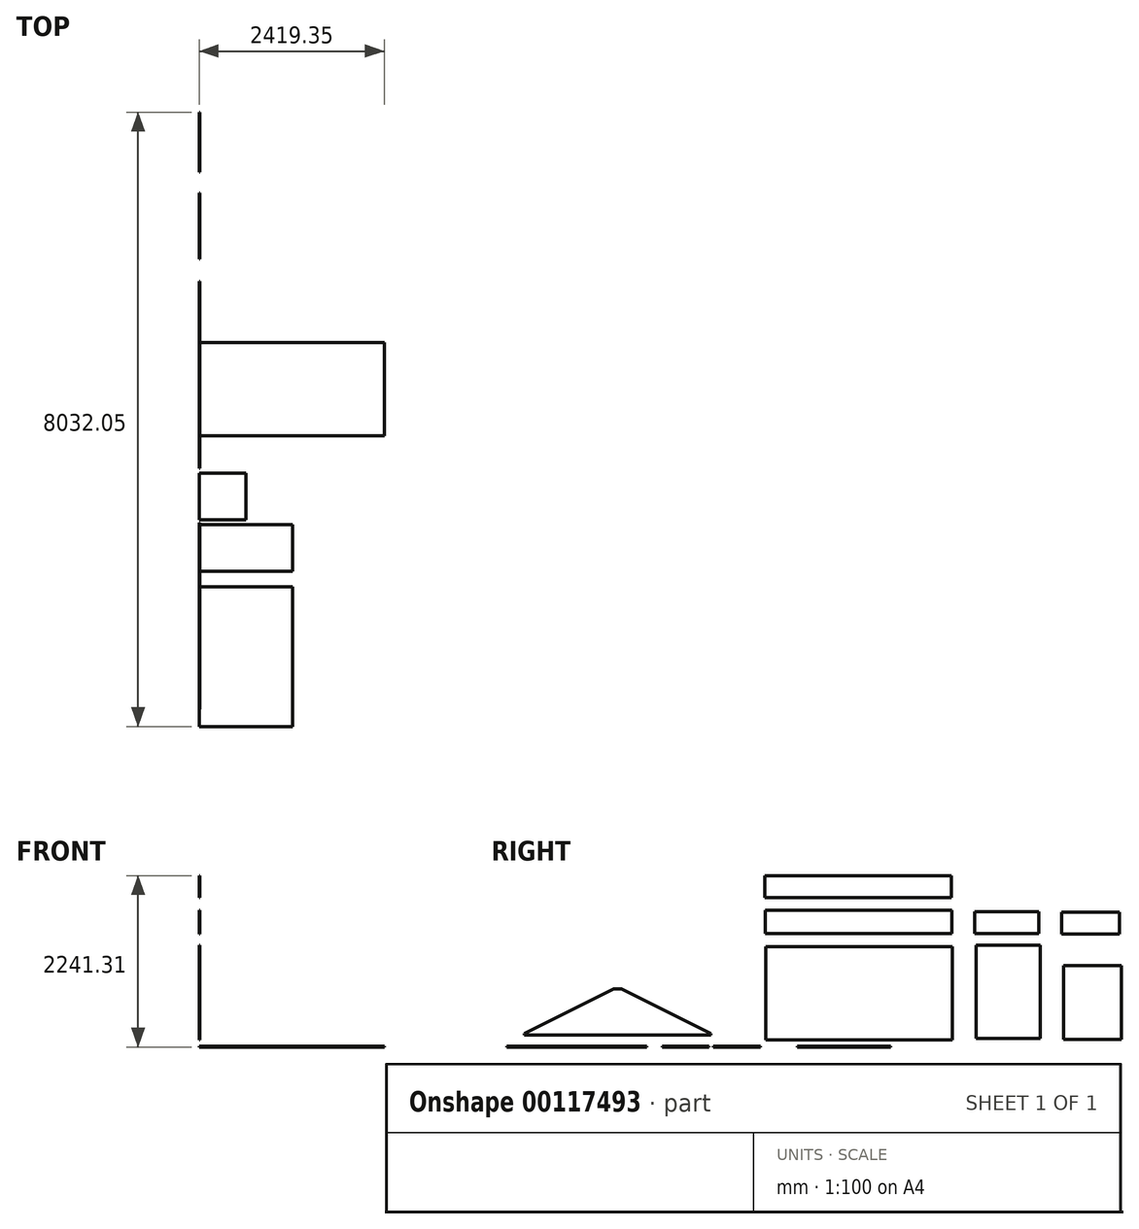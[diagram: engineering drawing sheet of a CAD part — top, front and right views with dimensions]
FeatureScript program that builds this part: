
annotation { "Feature Type Name" : "Feature", "Feature Type Description" : "" }
export const myFeature = defineFeature(function(context is Context, id is Id, definition is map)
    precondition{}
    {
        {
            var Q0;
            Q0=qCreatedBy(makeId("Top.planeOp"),FACE);
            var sketch = newSketch(context, id + "F0", { "sketchPlane" : qUnion([Q0])});
            skLineSegment(sketch, "E0.bottom", {"start": v(0, 0) * mm, "end": v(2419.35, 0) * mm});
            skLineSegment(sketch, "E0.top", {"start": v(0, -1219.2) * mm, "end": v(2419.35, -1219.2) * mm});
            skLineSegment(sketch, "E0.left", {"start": v(0, 0) * mm, "end": v(0, -1219.2) * mm});
            skLineSegment(sketch, "E0.right", {"start": v(2419.35, 0) * mm, "end": v(2419.35, -1219.2) * mm});
            skSolve(sketch);
        }
        {
            var Q0;
            Q0=makeQuery(id+"F0.imprint","IMPRINT",FACE,{"disambiguationData":[TD([[makeQuery(id+"F0.imprint","IMPRINT",EDGE,{"derivedFrom":sQuery(id+"F0.wireOp",EDGE,"E0.bottom")}),-1.0]])]});
            extrude(context, id + "F1", {"entities" : qUnion([Q0]), "depth" : 12.7 * mm});
        }
        {
            var Q0;
            Q0=qCreatedBy(makeId("Right.planeOp"),FACE);
            var sketch = newSketch(context, id + "F2", { "sketchPlane" : qUnion([Q0])});
            skLineSegment(sketch, "E1.bottom", {"start": v(-1635.37, 1309.76) * mm, "end": v(803.03, 1309.76) * mm});
            skLineSegment(sketch, "E1.top", {"start": v(-1635.37, 90.56) * mm, "end": v(803.03, 90.56) * mm});
            skLineSegment(sketch, "E1.left", {"start": v(-1635.37, 1309.76) * mm, "end": v(-1635.37, 90.56) * mm});
            skLineSegment(sketch, "E1.right", {"start": v(803.03, 1309.76) * mm, "end": v(803.03, 90.56) * mm});
            skSolve(sketch);
        }
        {
            var Q0;
            Q0=makeQuery(id+"F2.imprint","IMPRINT",FACE,{"disambiguationData":[TD([[makeQuery(id+"F2.imprint","IMPRINT",EDGE,{"derivedFrom":sQuery(id+"F2.wireOp",EDGE,"E1.bottom")}),-1.0]])]});
            extrude(context, id + "F3", {"entities" : qUnion([Q0]), "depth" : 9.52 * mm});
        }
        {
            var Q0;
            Q0=qCreatedBy(makeId("Right.planeOp"),FACE);
            var sketch = newSketch(context, id + "F4", { "sketchPlane" : qUnion([Q0])});
            skLineSegment(sketch, "E2.bottom", {"start": v(-1642.51, 1485.23) * mm, "end": v(795.89, 1485.23) * mm});
            skLineSegment(sketch, "E2.top", {"start": v(-1642.51, 1790.03) * mm, "end": v(795.89, 1790.03) * mm});
            skLineSegment(sketch, "E2.left", {"start": v(-1642.51, 1485.23) * mm, "end": v(-1642.51, 1790.03) * mm});
            skLineSegment(sketch, "E2.right", {"start": v(795.89, 1485.23) * mm, "end": v(795.89, 1790.03) * mm});
            skSolve(sketch);
        }
        {
            var Q0;
            Q0=makeQuery(id+"F4.imprint","IMPRINT",FACE,{"disambiguationData":[TD([[makeQuery(id+"F4.imprint","IMPRINT",EDGE,{"derivedFrom":sQuery(id+"F4.wireOp",EDGE,"E2.bottom")}),1.0]])]});
            extrude(context, id + "F5", {"entities" : qUnion([Q0]), "depth" : 9.52 * mm});
        }
        {
            var Q0;
            Q0=qCreatedBy(makeId("Right.planeOp"),FACE);
            var sketch = newSketch(context, id + "F6", { "sketchPlane" : qUnion([Q0])});
            skLineSegment(sketch, "E3.bottom", {"start": v(1117.42, 112.68) * mm, "end": v(1955.62, 112.68) * mm});
            skLineSegment(sketch, "E3.top", {"start": v(1117.42, 1331.88) * mm, "end": v(1955.62, 1331.88) * mm});
            skLineSegment(sketch, "E3.left", {"start": v(1117.42, 112.68) * mm, "end": v(1117.42, 1331.88) * mm});
            skLineSegment(sketch, "E3.right", {"start": v(1955.62, 112.68) * mm, "end": v(1955.62, 1331.88) * mm});
            skSolve(sketch);
        }
        {
            var Q0;
            Q0=makeQuery(id+"F6.imprint","IMPRINT",FACE,{"disambiguationData":[TD([[makeQuery(id+"F6.imprint","IMPRINT",EDGE,{"derivedFrom":sQuery(id+"F6.wireOp",EDGE,"E3.bottom")}),1.0]])]});
            extrude(context, id + "F7", {"entities" : qUnion([Q0]), "depth" : 9.52 * mm});
        }
        {
            var Q0;
            Q0=qCreatedBy(makeId("Right.planeOp"),FACE);
            var sketch = newSketch(context, id + "F8", { "sketchPlane" : qUnion([Q0])});
            skLineSegment(sketch, "E4.bottom", {"start": v(2256.7, 99.25) * mm, "end": v(3012.35, 99.25) * mm});
            skLineSegment(sketch, "E4.top", {"start": v(2256.7, 1064.45) * mm, "end": v(3012.35, 1064.45) * mm});
            skLineSegment(sketch, "E4.left", {"start": v(2256.7, 99.25) * mm, "end": v(2256.7, 1064.45) * mm});
            skLineSegment(sketch, "E4.right", {"start": v(3012.35, 99.25) * mm, "end": v(3012.35, 1064.45) * mm});
            skSolve(sketch);
        }
        {
            var Q0;
            Q0=makeQuery(id+"F8.imprint","IMPRINT",FACE,{"disambiguationData":[TD([[makeQuery(id+"F8.imprint","IMPRINT",EDGE,{"derivedFrom":sQuery(id+"F8.wireOp",EDGE,"E4.bottom")}),1.0]])]});
            extrude(context, id + "F9", {"entities" : qUnion([Q0]), "depth" : 9.52 * mm});
        }
        {
            var Q0;
            Q0=qCreatedBy(makeId("Right.planeOp"),FACE);
            var sketch = newSketch(context, id + "F10", { "sketchPlane" : qUnion([Q0])});
            skLineSegment(sketch, "E5.bottom", {"start": v(1095.24, 1484.8) * mm, "end": v(1933.44, 1484.8) * mm});
            skLineSegment(sketch, "E5.top", {"start": v(1095.24, 1770.56) * mm, "end": v(1933.44, 1770.56) * mm});
            skLineSegment(sketch, "E5.left", {"start": v(1095.24, 1484.8) * mm, "end": v(1095.24, 1770.56) * mm});
            skLineSegment(sketch, "E5.right", {"start": v(1933.44, 1484.8) * mm, "end": v(1933.44, 1770.56) * mm});
            skSolve(sketch);
        }
        {
            var Q0;
            Q0=makeQuery(id+"F10.imprint","IMPRINT",FACE,{"disambiguationData":[TD([[makeQuery(id+"F10.imprint","IMPRINT",EDGE,{"derivedFrom":sQuery(id+"F10.wireOp",EDGE,"E5.bottom")}),1.0]])]});
            extrude(context, id + "F11", {"entities" : qUnion([Q0]), "depth" : 9.52 * mm});
        }
        {
            var Q0;
            Q0=qCreatedBy(makeId("Right.planeOp"),FACE);
            var sketch = newSketch(context, id + "F12", { "sketchPlane" : qUnion([Q0])});
            skLineSegment(sketch, "E6.bottom", {"start": v(2231.6, 1474.91) * mm, "end": v(2987.25, 1474.91) * mm});
            skLineSegment(sketch, "E6.top", {"start": v(2231.6, 1760.66) * mm, "end": v(2987.25, 1760.66) * mm});
            skLineSegment(sketch, "E6.left", {"start": v(2231.6, 1474.91) * mm, "end": v(2231.6, 1760.66) * mm});
            skLineSegment(sketch, "E6.right", {"start": v(2987.25, 1474.91) * mm, "end": v(2987.25, 1760.66) * mm});
            skSolve(sketch);
        }
        {
            var Q0;
            Q0=makeQuery(id+"F12.imprint","IMPRINT",FACE,{"disambiguationData":[TD([[makeQuery(id+"F12.imprint","IMPRINT",EDGE,{"derivedFrom":sQuery(id+"F12.wireOp",EDGE,"E6.bottom")}),1.0]])]});
            extrude(context, id + "F13", {"entities" : qUnion([Q0]), "depth" : 9.52 * mm});
        }
        {
            var Q0;
            Q0=qCreatedBy(makeId("Top.planeOp"),FACE);
            var sketch = newSketch(context, id + "F14", { "sketchPlane" : qUnion([Q0])});
            skLineSegment(sketch, "E7.bottom", {"start": v(0, -2379.66) * mm, "end": v(1219.2, -2379.66) * mm});
            skLineSegment(sketch, "E7.top", {"start": v(0, -2989.26) * mm, "end": v(1219.2, -2989.26) * mm});
            skLineSegment(sketch, "E7.left", {"start": v(0, -2379.66) * mm, "end": v(0, -2989.26) * mm});
            skLineSegment(sketch, "E7.right", {"start": v(1219.2, -2379.66) * mm, "end": v(1219.2, -2989.26) * mm});
            skSolve(sketch);
        }
        {
            var Q0;
            Q0=qCreatedBy(makeId("Top.planeOp"),FACE);
            var sketch = newSketch(context, id + "F15", { "sketchPlane" : qUnion([Q0])});
            skLineSegment(sketch, "E8.bottom", {"start": v(0, -3190.9) * mm, "end": v(1219.2, -3190.9) * mm});
            skLineSegment(sketch, "E8.top", {"start": v(0, -5019.7) * mm, "end": v(1219.2, -5019.7) * mm});
            skLineSegment(sketch, "E8.left", {"start": v(0, -3190.9) * mm, "end": v(0, -5019.7) * mm});
            skLineSegment(sketch, "E8.right", {"start": v(1219.2, -3190.9) * mm, "end": v(1219.2, -5019.7) * mm});
            skSolve(sketch);
        }
        {
            var Q0;
            Q0=makeQuery(id+"F15.imprint","IMPRINT",FACE,{"disambiguationData":[TD([[makeQuery(id+"F15.imprint","IMPRINT",EDGE,{"derivedFrom":sQuery(id+"F15.wireOp",EDGE,"E8.bottom")}),-1.0]])]});
            extrude(context, id + "F16", {"entities" : qUnion([Q0]), "depth" : 9.52 * mm});
        }
        {
            var Q0;
            Q0=makeQuery(id+"F14.imprint","IMPRINT",FACE,{"disambiguationData":[TD([[makeQuery(id+"F14.imprint","IMPRINT",EDGE,{"derivedFrom":sQuery(id+"F14.wireOp",EDGE,"E7.bottom")}),-1.0]])]});
            extrude(context, id + "F17", {"entities" : qUnion([Q0]), "depth" : 9.52 * mm});
        }
        {
            var Q0;
            Q0=qCreatedBy(makeId("Top.planeOp"),FACE);
            var sketch = newSketch(context, id + "F18", { "sketchPlane" : qUnion([Q0])});
            skLineSegment(sketch, "E9.bottom", {"start": v(0, -2315.98) * mm, "end": v(609.6, -2315.98) * mm});
            skLineSegment(sketch, "E9.top", {"start": v(0, -1706.38) * mm, "end": v(609.6, -1706.38) * mm});
            skLineSegment(sketch, "E9.left", {"start": v(0, -2315.98) * mm, "end": v(0, -1706.38) * mm});
            skLineSegment(sketch, "E9.right", {"start": v(609.6, -2315.98) * mm, "end": v(609.6, -1706.38) * mm});
            skSolve(sketch);
        }
        {
            var Q0;
            Q0=makeQuery(id+"F18.imprint","IMPRINT",FACE,{"disambiguationData":[TD([[makeQuery(id+"F18.imprint","IMPRINT",EDGE,{"derivedFrom":sQuery(id+"F18.wireOp",EDGE,"E9.bottom")}),1.0]])]});
            extrude(context, id + "F19", {"entities" : qUnion([Q0]), "depth" : 9.52 * mm});
        }
        {
            var Q0;
            Q0=qCreatedBy(makeId("Right.planeOp"),FACE);
            var sketch = newSketch(context, id + "F20", { "sketchPlane" : qUnion([Q0])});
            skLineSegment(sketch, "E10", {"start": v(-4790.86, 176.8) * mm, "end": v(-3624.12, 758.52) * mm});
            skLineSegment(sketch, "E11", {"start": v(-3519.21, 758.52) * mm, "end": v(-2352.46, 176.8) * mm});
            skLineSegment(sketch, "E12", {"start": v(-4790.86, 176.8) * mm, "end": v(-4790.86, 157.75) * mm});
            skLineSegment(sketch, "E13", {"start": v(-4790.86, 157.75) * mm, "end": v(-2352.46, 157.75) * mm});
            skLineSegment(sketch, "E14", {"start": v(-2352.46, 157.75) * mm, "end": v(-2352.46, 176.8) * mm});
            skLineSegment(sketch, "E15", {"start": v(-3624.12, 758.52) * mm, "end": v(-3519.21, 758.52) * mm});
            skSolve(sketch);
        }
        {
            var Q0;
            Q0 = qSketchRegion(id + "F20", true);
            extrude(context, id + "F21", {"entities" : qUnion([Q0]), "depth" : 9.52 * mm});
        }
        {
            var Q0;
            Q0=qCreatedBy(makeId("Right.planeOp"),FACE);
            var sketch = newSketch(context, id + "F22", { "sketchPlane" : qUnion([Q0])});
            skLineSegment(sketch, "E16.bottom", {"start": v(-1647.36, 1955.56) * mm, "end": v(791.04, 1955.56) * mm});
            skLineSegment(sketch, "E16.top", {"start": v(-1647.36, 2241.31) * mm, "end": v(791.04, 2241.31) * mm});
            skLineSegment(sketch, "E16.left", {"start": v(-1647.36, 1955.56) * mm, "end": v(-1647.36, 2241.31) * mm});
            skLineSegment(sketch, "E16.right", {"start": v(791.04, 1955.56) * mm, "end": v(791.04, 2241.31) * mm});
            skSolve(sketch);
        }
        {
            var Q0;
            Q0=makeQuery(id+"F22.imprint","IMPRINT",FACE,{"disambiguationData":[TD([[makeQuery(id+"F22.imprint","IMPRINT",EDGE,{"derivedFrom":sQuery(id+"F22.wireOp",EDGE,"E16.bottom")}),1.0]])]});
            extrude(context, id + "F23", {"entities" : qUnion([Q0]), "depth" : 9.52 * mm});
        }
    });
